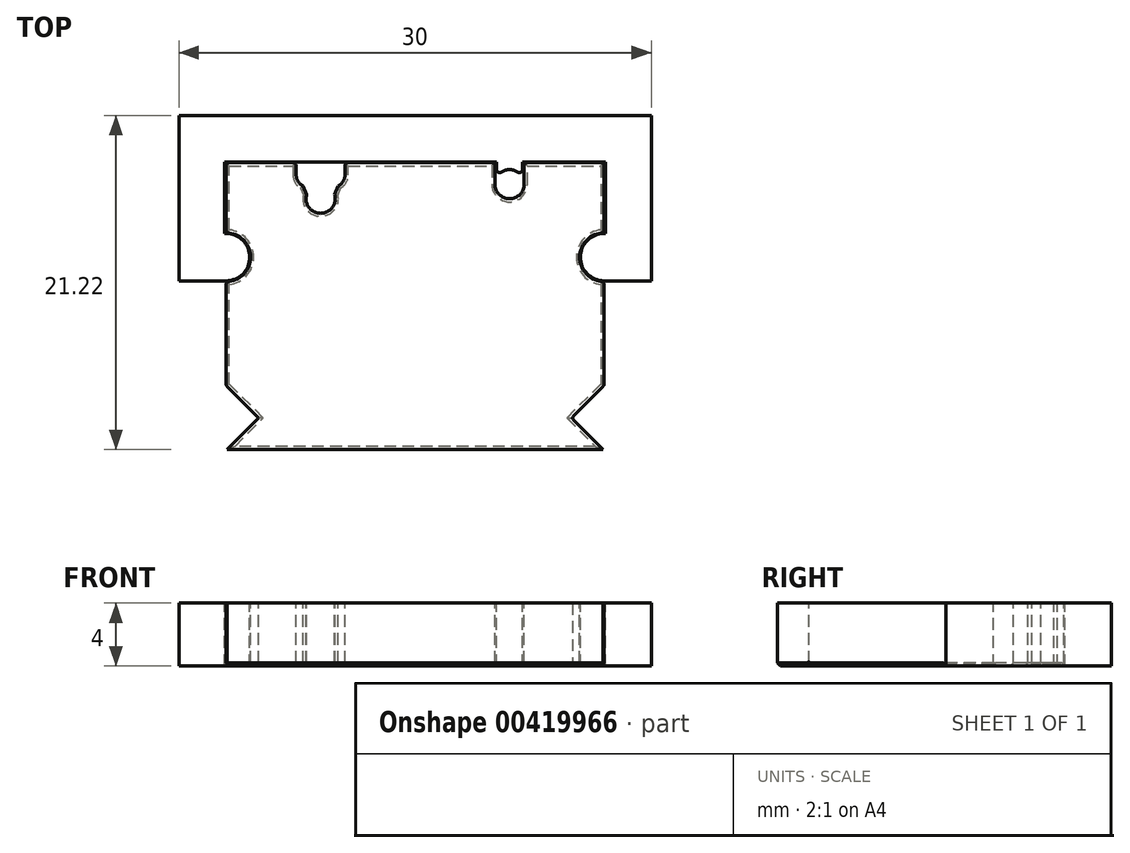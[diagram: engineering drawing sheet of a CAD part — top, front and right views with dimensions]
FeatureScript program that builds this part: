
annotation { "Feature Type Name" : "Feature", "Feature Type Description" : "" }
export const myFeature = defineFeature(function(context is Context, id is Id, definition is map)
    precondition{}
    {
        {
            var Q0;
            Q0=qCreatedBy(makeId("Top.planeOp"),FACE);
            var sketch = newSketch(context, id + "F0", { "sketchPlane" : qUnion([Q0])});
            skCircle(sketch, "E0", {"center": v(-6, 0) * mm, "radius": 0.92 * mm, "construction": true});
            skCircle(sketch, "E1", {"center": v(-6.77, 1.51) * mm, "radius": 0.78 * mm, "construction": true});
            skCircle(sketch, "E2", {"center": v(-5.22, 1.51) * mm, "radius": 0.78 * mm, "construction": true});
            skLineSegment(sketch, "E3", {"start": v(-12, -15.92) * mm, "end": v(12, -15.92) * mm});
            skLineSegment(sketch, "E4", {"start": v(-12, -11.93) * mm, "end": v(-12, -5.26) * mm});
            skLineSegment(sketch, "E5", {"start": v(12, 2.29) * mm, "end": v(12, -2.16) * mm});
            skLineSegment(sketch, "E6", {"start": v(-12, 2.29) * mm, "end": v(12, 2.29) * mm, "construction": true});
            skLineSegment(sketch, "E7", {"start": v(-7.55, 1.51) * mm, "end": v(-7.55, 2.29) * mm});
            skLineSegment(sketch, "E8", {"start": v(-4.45, 1.51) * mm, "end": v(-4.45, 2.29) * mm});
            skLineSegment(sketch, "E9", {"start": v(-7.55, 2.29) * mm, "end": v(-12, 2.29) * mm});
            skCircle(sketch, "E10", {"center": v(6, 0.92) * mm, "radius": 0.92 * mm, "construction": true});
            skLineSegment(sketch, "E11", {"start": v(5.07, 0.92) * mm, "end": v(5.07, 2.29) * mm});
            skLineSegment(sketch, "E12", {"start": v(5.07, 2.29) * mm, "end": v(-4.45, 2.29) * mm});
            skLineSegment(sketch, "E13", {"start": v(6.92, 0.92) * mm, "end": v(6.92, 2.29) * mm});
            skLineSegment(sketch, "E14", {"start": v(6.92, 2.29) * mm, "end": v(12, 2.29) * mm});
            skArc(sketch, "E15", {"start": v(5.08, 0.92) * mm, "mid": v(6, 0) * mm, "end": v(6.93, 0.92) * mm});
            skLineSegment(sketch, "E16", {"start": v(-7.11, 0.82) * mm, "end": v(-6.89, 0.26) * mm});
            skLineSegment(sketch, "E17", {"start": v(-4.89, 0.82) * mm, "end": v(-5.11, 0.26) * mm});
            skArc(sketch, "E18", {"start": v(-6.89, 0.26) * mm, "mid": v(-6, -0.93) * mm, "end": v(-5.11, 0.26) * mm});
            skArc(sketch, "E19", {"start": v(-7.55, 1.51) * mm, "mid": v(-7.43, 1.1) * mm, "end": v(-7.11, 0.82) * mm});
            skArc(sketch, "E20", {"start": v(-4.45, 1.51) * mm, "mid": v(-4.57, 1.1) * mm, "end": v(-4.89, 0.82) * mm});
            skLineSegment(sketch, "E21", {"start": v(-7.5, 1.22) * mm, "end": v(-6.86, -0.35) * mm, "construction": true});
            skLineSegment(sketch, "E22", {"start": v(-5.14, -0.35) * mm, "end": v(-4.5, 1.22) * mm, "construction": true});
            skLineSegment(sketch, "E23", {"start": v(-6, 0.92) * mm, "end": v(6, 0.92) * mm, "construction": true});
            skLineSegment(sketch, "E24", {"start": v(-12, -11.93) * mm, "end": v(-10, -13.93) * mm, "construction": true});
            skLineSegment(sketch, "E25", {"start": v(-10, -13.93) * mm, "end": v(-12, -15.93) * mm, "construction": true});
            skLineSegment(sketch, "E26.0", {"start": v(-9.93, -13.93) * mm, "end": v(-11.93, -15.92) * mm});
            skLineSegment(sketch, "E26.1", {"start": v(-12, -11.85) * mm, "end": v(-9.93, -13.93) * mm});
            skLineSegment(sketch, "E27.MirrorCS", {"start": v(12, -11.85) * mm, "end": v(9.93, -13.93) * mm});
            skLineSegment(sketch, "E28.MirrorCS", {"start": v(9.93, -13.93) * mm, "end": v(11.93, -15.92) * mm});
            skArc(sketch, "E29", {"start": v(-12, -2.16) * mm, "mid": v(-10.45, -3.71) * mm, "end": v(-12, -5.26) * mm});
            skLineSegment(sketch, "E30.trimOffspring", {"start": v(-12, -2.16) * mm, "end": v(-12, 2.29) * mm});
            skArc(sketch, "E31.MirrorCS", {"start": v(12, -2.16) * mm, "mid": v(10.45, -3.71) * mm, "end": v(12, -5.26) * mm});
            skLineSegment(sketch, "E32.trimOffspring", {"start": v(12, -5.26) * mm, "end": v(12, -11.85) * mm});
            skSolve(sketch);
        }
        {
            var Q0;
            Q0=qCreatedBy(makeId("Front.planeOp"),FACE);
            var sketch = newSketch(context, id + "F1", { "sketchPlane" : qUnion([Q0])});
            skLineSegment(sketch, "E33", {"start": v(0, 0) * mm, "end": v(0, 4) * mm});
            skSolve(sketch);
        }
        {
            var Q0;
            Q0=makeQuery(id+"F0.imprint","IMPRINT",FACE,{"disambiguationData":[TD([[makeQuery(id+"F0.imprint","IMPRINT",EDGE,{"derivedFrom":sQuery(id+"F0.wireOp",EDGE,"E5")}),-1.0]])]});
            var Q1;
            Q1=sQuery(id+"F1.wireOp",EDGE,"E33");
            sweep(context, id + "F2", {"profiles" : qUnion([Q0]), "path" : qUnion([Q1])});
        }
        {
            var Q0;
            Q0=makeQuery(id+"F2.opSweep","CAP_FACE",FACE,{"disambiguationData":[OSD([sQuery(id+"F0.wireOp",EDGE,"E3"),sQuery(id+"F0.wireOp",EDGE,"E4"),sQuery(id+"F0.wireOp",EDGE,"E5"),sQuery(id+"F0.wireOp",EDGE,"E7"),sQuery(id+"F0.wireOp",EDGE,"E8"),sQuery(id+"F0.wireOp",EDGE,"E9"),sQuery(id+"F0.wireOp",EDGE,"E11"),sQuery(id+"F0.wireOp",EDGE,"E12"),sQuery(id+"F0.wireOp",EDGE,"E13"),sQuery(id+"F0.wireOp",EDGE,"E14"),sQuery(id+"F0.wireOp",EDGE,"E15"),sQuery(id+"F0.wireOp",EDGE,"E16"),sQuery(id+"F0.wireOp",EDGE,"E17"),sQuery(id+"F0.wireOp",EDGE,"E18"),sQuery(id+"F0.wireOp",EDGE,"E19"),sQuery(id+"F0.wireOp",EDGE,"E20"),sQuery(id+"F1.wireOp",VERTEX,"E33.start")])],"isStart":true});
            chamfer(context, id + "F3", {"entities" : qUnion([Q0]), "width" : 0.2 * mm});
        }
        {
            var Q0;
            Q0=qCreatedBy(makeId("Top.planeOp"),FACE);
            var sketch = newSketch(context, id + "F4", { "sketchPlane" : qUnion([Q0])});
            skPoint(sketch, "E34.0", {"position": v(-12, 2.29) * mm});
            skPoint(sketch, "E35.0", {"position": v(-12, -3.71) * mm});
            skArc(sketch, "E36", {"start": v(-12, -2.21) * mm, "mid": v(-10.5, -3.71) * mm, "end": v(-12, -5.21) * mm});
            skLineSegment(sketch, "E37", {"start": v(-12, -2.21) * mm, "end": v(-12.1, -2.21) * mm});
            skLineSegment(sketch, "E38", {"start": v(-12.1, -2.21) * mm, "end": v(-12.1, 2.34) * mm});
            skLineSegment(sketch, "E39", {"start": v(-12.1, 2.34) * mm, "end": v(0, 2.34) * mm});
            skLineSegment(sketch, "E40", {"start": v(-12, -5.21) * mm, "end": v(-15, -5.21) * mm});
            skLineSegment(sketch, "E41", {"start": v(-15, -5.21) * mm, "end": v(-15, 5.29) * mm});
            skLineSegment(sketch, "E42", {"start": v(-15, 5.29) * mm, "end": v(0, 5.29) * mm});
            skLineSegment(sketch, "E43.MirrorCS", {"start": v(15, 5.29) * mm, "end": v(0, 5.29) * mm});
            skLineSegment(sketch, "E44.MirrorCS", {"start": v(12.1, 2.34) * mm, "end": v(0, 2.34) * mm});
            skLineSegment(sketch, "E45.MirrorCS", {"start": v(15, -5.21) * mm, "end": v(15, 5.29) * mm});
            skLineSegment(sketch, "E46.MirrorCS", {"start": v(12.1, -2.21) * mm, "end": v(12.1, 2.34) * mm});
            skLineSegment(sketch, "E47.MirrorCS", {"start": v(12, -5.21) * mm, "end": v(15, -5.21) * mm});
            skArc(sketch, "E48.MirrorCS", {"start": v(12, -2.21) * mm, "mid": v(10.5, -3.71) * mm, "end": v(12, -5.21) * mm});
            skLineSegment(sketch, "E49.MirrorCS", {"start": v(12, -2.21) * mm, "end": v(12.1, -2.21) * mm});
            skLineSegment(sketch, "E50", {"start": v(5.17, 2.34) * mm, "end": v(5.17, 1.34) * mm});
            skPoint(sketch, "E51.0", {"position": v(6, 0.92) * mm});
            skCircle(sketch, "E52.0", {"center": v(6, 0.92) * mm, "radius": 0.92 * mm, "construction": true});
            skArc(sketch, "E53", {"start": v(5.17, 1.34) * mm, "mid": v(6, 1.85) * mm, "end": v(6.83, 1.34) * mm});
            skLineSegment(sketch, "E54", {"start": v(6.83, 1.34) * mm, "end": v(6.83, 2.34) * mm});
            skSolve(sketch);
        }
        {
            var Q0;
            Q0 = qSketchRegion(id + "F4", true);
            var Q1;
            Q1=sQuery(id+"F1.wireOp",EDGE,"E33");
            sweep(context, id + "F5", {"profiles" : qUnion([Q0]), "path" : qUnion([Q1])});
        }
        {
            var Q0;
            Q0=makeQuery(id+"F2.opSweep","SWEPT_EDGE",EDGE,{"disambiguationData":[OSD([sQuery(id+"F0.wireOp",EDGE,"E4"),sQuery(id+"F0.wireOp",EDGE,"E9"),sQuery(id+"F1.wireOp",EDGE,"E33")])]});
            var Q1;
            Q1=makeQuery(id+"F2.opSweep","SWEPT_EDGE",EDGE,{"disambiguationData":[OSD([sQuery(id+"F0.wireOp",EDGE,"E4"),sQuery(id+"F0.wireOp",EDGE,"E26.1"),sQuery(id+"F1.wireOp",EDGE,"E33")])]});
            var Q2;
            Q2=makeQuery(id+"F2.opSweep","SWEPT_EDGE",EDGE,{"disambiguationData":[OSD([sQuery(id+"F0.wireOp",EDGE,"E5"),sQuery(id+"F0.wireOp",EDGE,"E14"),sQuery(id+"F1.wireOp",EDGE,"E33")])]});
            var Q3;
            Q3=makeQuery(id+"F2.opSweep","SWEPT_EDGE",EDGE,{"disambiguationData":[OSD([sQuery(id+"F0.wireOp",EDGE,"E5"),sQuery(id+"F0.wireOp",EDGE,"E27.MirrorCS"),sQuery(id+"F1.wireOp",EDGE,"E33")])]});
            var Q4;
            Q4=makeQuery(id+"F2.opSweep","SWEPT_EDGE",EDGE,{"disambiguationData":[OSD([sQuery(id+"F0.wireOp",EDGE,"E4"),sQuery(id+"F0.wireOp",EDGE,"E9"),sQuery(id+"F1.wireOp",EDGE,"E33")])]});
            var Q5;
            Q5=makeQuery(id+"F2.opSweep","SWEPT_EDGE",EDGE,{"disambiguationData":[OSD([sQuery(id+"F0.wireOp",EDGE,"E7"),sQuery(id+"F0.wireOp",EDGE,"E9"),sQuery(id+"F1.wireOp",EDGE,"E33")])]});
            var Q6;
            Q6=makeQuery(id+"F2.opSweep","SWEPT_EDGE",EDGE,{"disambiguationData":[OSD([sQuery(id+"F0.wireOp",EDGE,"E8"),sQuery(id+"F0.wireOp",EDGE,"E12"),sQuery(id+"F1.wireOp",EDGE,"E33")])]});
            var Q7;
            Q7=makeQuery(id+"F2.opSweep","SWEPT_EDGE",EDGE,{"disambiguationData":[OSD([sQuery(id+"F0.wireOp",EDGE,"E11"),sQuery(id+"F0.wireOp",EDGE,"E12"),sQuery(id+"F1.wireOp",EDGE,"E33")])]});
            var Q8;
            Q8=makeQuery(id+"F2.opSweep","SWEPT_EDGE",EDGE,{"disambiguationData":[OSD([sQuery(id+"F0.wireOp",EDGE,"E13"),sQuery(id+"F0.wireOp",EDGE,"E14"),sQuery(id+"F1.wireOp",EDGE,"E33")])]});
            var Q9;
            Q9=makeQuery(id+"F2.opSweep","SWEPT_EDGE",EDGE,{"disambiguationData":[OSD([sQuery(id+"F0.wireOp",EDGE,"E5"),sQuery(id+"F0.wireOp",EDGE,"E14"),sQuery(id+"F1.wireOp",EDGE,"E33")])]});
            var Q10;
            Q10=makeQuery(id+"F2.opSweep","SWEPT_EDGE",EDGE,{"disambiguationData":[OSD([sQuery(id+"F0.wireOp",EDGE,"E4"),sQuery(id+"F0.wireOp",EDGE,"E9"),sQuery(id+"F1.wireOp",EDGE,"E33")])]});
            var Q11;
            Q11=makeQuery(id+"F2.opSweep","SWEPT_EDGE",EDGE,{"disambiguationData":[OSD([sQuery(id+"F0.wireOp",EDGE,"E4"),sQuery(id+"F0.wireOp",EDGE,"E26.1"),sQuery(id+"F1.wireOp",EDGE,"E33")])]});
            var Q12;
            Q12=makeQuery(id+"F2.opSweep","SWEPT_EDGE",EDGE,{"disambiguationData":[OSD([sQuery(id+"F0.wireOp",EDGE,"E29"),sQuery(id+"F0.wireOp",EDGE,"E30.trimOffspring"),sQuery(id+"F1.wireOp",EDGE,"E33")])]});
            var Q13;
            Q13=makeQuery(id+"F2.opSweep","SWEPT_EDGE",EDGE,{"disambiguationData":[OSD([sQuery(id+"F0.wireOp",EDGE,"E31.MirrorCS"),sQuery(id+"F0.wireOp",EDGE,"E32.trimOffspring"),sQuery(id+"F1.wireOp",EDGE,"E33")])]});
            var Q14;
            Q14=makeQuery(id+"F5.opSweep","SWEPT_EDGE",EDGE,{"disambiguationData":[OSD([sQuery(id+"F1.wireOp",EDGE,"E33"),sQuery(id+"F4.wireOp",EDGE,"E50"),sQuery(id+"F4.wireOp",EDGE,"E53")])]});
            var Q15;
            Q15=makeQuery(id+"F5.opSweep","SWEPT_EDGE",EDGE,{"disambiguationData":[OSD([sQuery(id+"F1.wireOp",EDGE,"E33"),sQuery(id+"F4.wireOp",EDGE,"E53"),sQuery(id+"F4.wireOp",EDGE,"E54")])]});
            fillet(context, id + "F6", {"entities" : qUnion([Q0, Q1, Q2, Q3, Q4, Q5, Q6, Q7, Q8, Q9, Q10, Q11, Q12, Q13, Q14, Q15]), "radius" : 0.2 * mm, "allowEdgeOverflow" : false});
        }
    });
